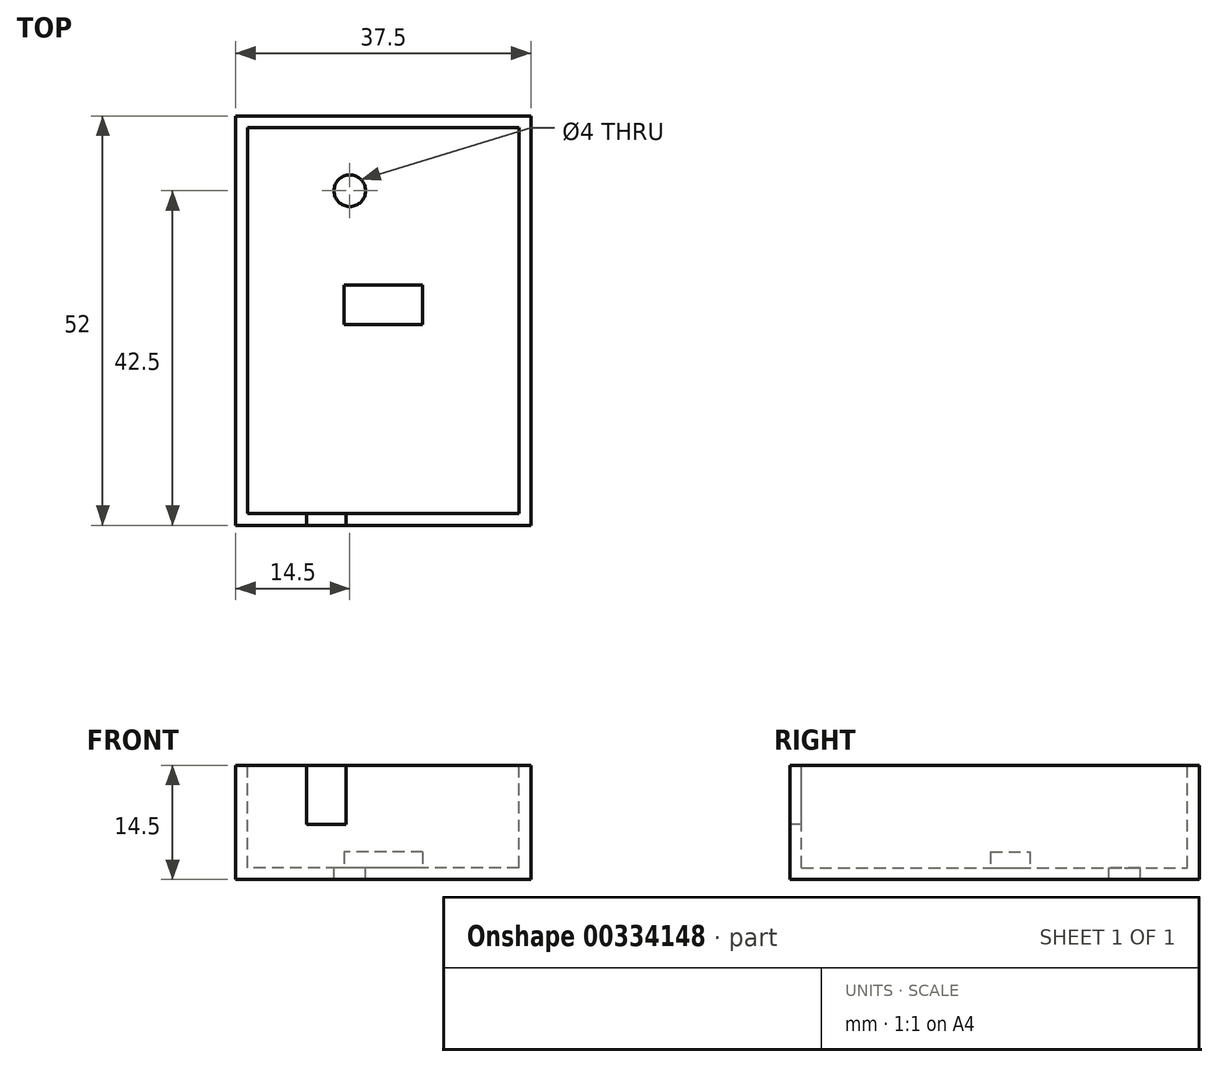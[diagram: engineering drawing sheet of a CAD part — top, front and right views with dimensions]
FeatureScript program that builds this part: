
annotation { "Feature Type Name" : "Feature", "Feature Type Description" : "" }
export const myFeature = defineFeature(function(context is Context, id is Id, definition is map)
    precondition{}
    {
        {
            var Q0;
            Q0=qCreatedBy(makeId("Top.planeOp"),FACE);
            var sketch = newSketch(context, id + "F0", { "sketchPlane" : qUnion([Q0])});
            skLineSegment(sketch, "E0.bottom", {"start": v(18.75, -26) * mm, "end": v(-18.75, -26) * mm});
            skLineSegment(sketch, "E0.top", {"start": v(18.75, 26) * mm, "end": v(-18.75, 26) * mm});
            skLineSegment(sketch, "E0.left", {"start": v(18.75, -26) * mm, "end": v(18.75, 26) * mm});
            skLineSegment(sketch, "E0.right", {"start": v(-18.75, -26) * mm, "end": v(-18.75, 26) * mm});
            skPoint(sketch, "E0.middle", {"position": v(0, 0) * mm});
            skSolve(sketch);
        }
        {
            var Q0;
            Q0 = qSketchRegion(id + "F0", true);
            extrude(context, id + "F1", {"entities" : qUnion([Q0]), "depth" : 14.5 * mm});
        }
        {
            var Q0;
            Q0=makeQuery(id+"F1.opExtrude","CAP_FACE",FACE,{"disambiguationData":[OSD([sQuery(id+"F0.wireOp",EDGE,"E0.bottom"),sQuery(id+"F0.wireOp",EDGE,"E0.top"),sQuery(id+"F0.wireOp",EDGE,"E0.left"),sQuery(id+"F0.wireOp",EDGE,"E0.right")])],"isStart":false});
            var sketch = newSketch(context, id + "F2", { "sketchPlane" : qUnion([Q0])});
            skLineSegment(sketch, "E1.bottom", {"start": v(17.25, -24.5) * mm, "end": v(-17.25, -24.5) * mm});
            skLineSegment(sketch, "E1.top", {"start": v(17.25, 24.5) * mm, "end": v(-17.25, 24.5) * mm});
            skLineSegment(sketch, "E1.left", {"start": v(17.25, -24.5) * mm, "end": v(17.25, 24.5) * mm});
            skLineSegment(sketch, "E1.right", {"start": v(-17.25, -24.5) * mm, "end": v(-17.25, 24.5) * mm});
            skPoint(sketch, "E1.middle", {"position": v(0, 0) * mm});
            skSolve(sketch);
        }
        {
            var Q0;
            Q0 = qSketchRegion(id + "F2", true);
            extrude(context, id + "F3", {"entities" : qUnion([Q0]), "operationType" : NewBodyOperationType.REMOVE, "oppositeDirection" : true, "depth" : 13 * mm});
        }
        {
            var Q0;
            Q0=makeQuery(id+"F3.boolean.opBoolean","COPY",FACE,{"derivedFrom":makeQuery(id+"F3.opExtrude","CAP_FACE",FACE,{"disambiguationData":[OSD([sQuery(id+"F2.wireOp",EDGE,"E1.bottom"),sQuery(id+"F2.wireOp",EDGE,"E1.top"),sQuery(id+"F2.wireOp",EDGE,"E1.left"),sQuery(id+"F2.wireOp",EDGE,"E1.right")])],"isStart":false})});
            var sketch = newSketch(context, id + "F4", { "sketchPlane" : qUnion([Q0])});
            skCircle(sketch, "E2", {"center": v(-4.25, 16.5) * mm, "radius": 2 * mm});
            skSolve(sketch);
        }
        {
            var Q0;
            Q0 = qSketchRegion(id + "F4", true);
            extrude(context, id + "F5", {"entities" : qUnion([Q0]), "operationType" : NewBodyOperationType.REMOVE, "oppositeDirection" : true, "depth" : 25 * mm});
        }
        {
            var Q0;
            Q0=makeQuery(id+"F3.boolean.opBoolean","COPY",FACE,{"derivedFrom":makeQuery(id+"F3.opExtrude","CAP_FACE",FACE,{"disambiguationData":[OSD([sQuery(id+"F2.wireOp",EDGE,"E1.bottom"),sQuery(id+"F2.wireOp",EDGE,"E1.top"),sQuery(id+"F2.wireOp",EDGE,"E1.left"),sQuery(id+"F2.wireOp",EDGE,"E1.right")])],"isStart":false})});
            var sketch = newSketch(context, id + "F6", { "sketchPlane" : qUnion([Q0])});
            skLineSegment(sketch, "E3.bottom", {"start": v(5, -0.5) * mm, "end": v(-5, -0.5) * mm});
            skLineSegment(sketch, "E3.top", {"start": v(5, 4.5) * mm, "end": v(-5, 4.5) * mm});
            skLineSegment(sketch, "E3.left", {"start": v(5, -0.5) * mm, "end": v(5, 4.5) * mm});
            skLineSegment(sketch, "E3.right", {"start": v(-5, -0.5) * mm, "end": v(-5, 4.5) * mm});
            skPoint(sketch, "E3.middle", {"position": v(0, 2) * mm});
            skSolve(sketch);
        }
        {
            var Q0;
            Q0 = qSketchRegion(id + "F6", true);
            extrude(context, id + "F7", {"entities" : qUnion([Q0]), "operationType" : NewBodyOperationType.ADD, "depth" : 2 * mm});
        }
        {
            var Q0;
            Q0=makeQuery(id+"F1.opExtrude","SWEPT_FACE",FACE,{"disambiguationData":[OSD([sQuery(id+"F0.wireOp",EDGE,"E0.bottom")])]});
            var sketch = newSketch(context, id + "F8", { "sketchPlane" : qUnion([Q0])});
            skLineSegment(sketch, "E4.bottom", {"start": v(-4.75, 14.5) * mm, "end": v(-9.75, 14.5) * mm});
            skLineSegment(sketch, "E4.top", {"start": v(-4.75, 7) * mm, "end": v(-9.75, 7) * mm});
            skLineSegment(sketch, "E4.left", {"start": v(-4.75, 14.5) * mm, "end": v(-4.75, 7) * mm});
            skLineSegment(sketch, "E4.right", {"start": v(-9.75, 14.5) * mm, "end": v(-9.75, 7) * mm});
            skSolve(sketch);
        }
        {
            var Q0;
            Q0 = qSketchRegion(id + "F8", true);
            extrude(context, id + "F9", {"entities" : qUnion([Q0]), "operationType" : NewBodyOperationType.REMOVE, "oppositeDirection" : true, "depth" : 10 * mm});
        }
    });
